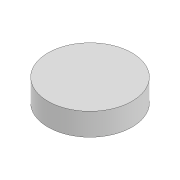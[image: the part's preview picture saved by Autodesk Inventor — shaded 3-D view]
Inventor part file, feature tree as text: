
AUTODESK INVENTOR PART (.ipt)
format: ipt  version: 2020 (Build 240168000, 168)  size: 74,752 bytes
history: native  units: mm
features: other x1, extrude x1, sketch x1
ambient origin geometry x8: Origin, YZ Plane, XZ Plane, XY Plane, X Axis, Y Axis, Z Axis, Center Point
bodies: Body1 (feature_tree)
feature tree (3):
  other  "Sólido1"
  extrude  "Extrusão1"  Depth=12.0mm TaperAngle=0.0deg
  sketch  "Esboço1"  dims[d0=44.9mm d1=12.0mm d2=0.0mm]
